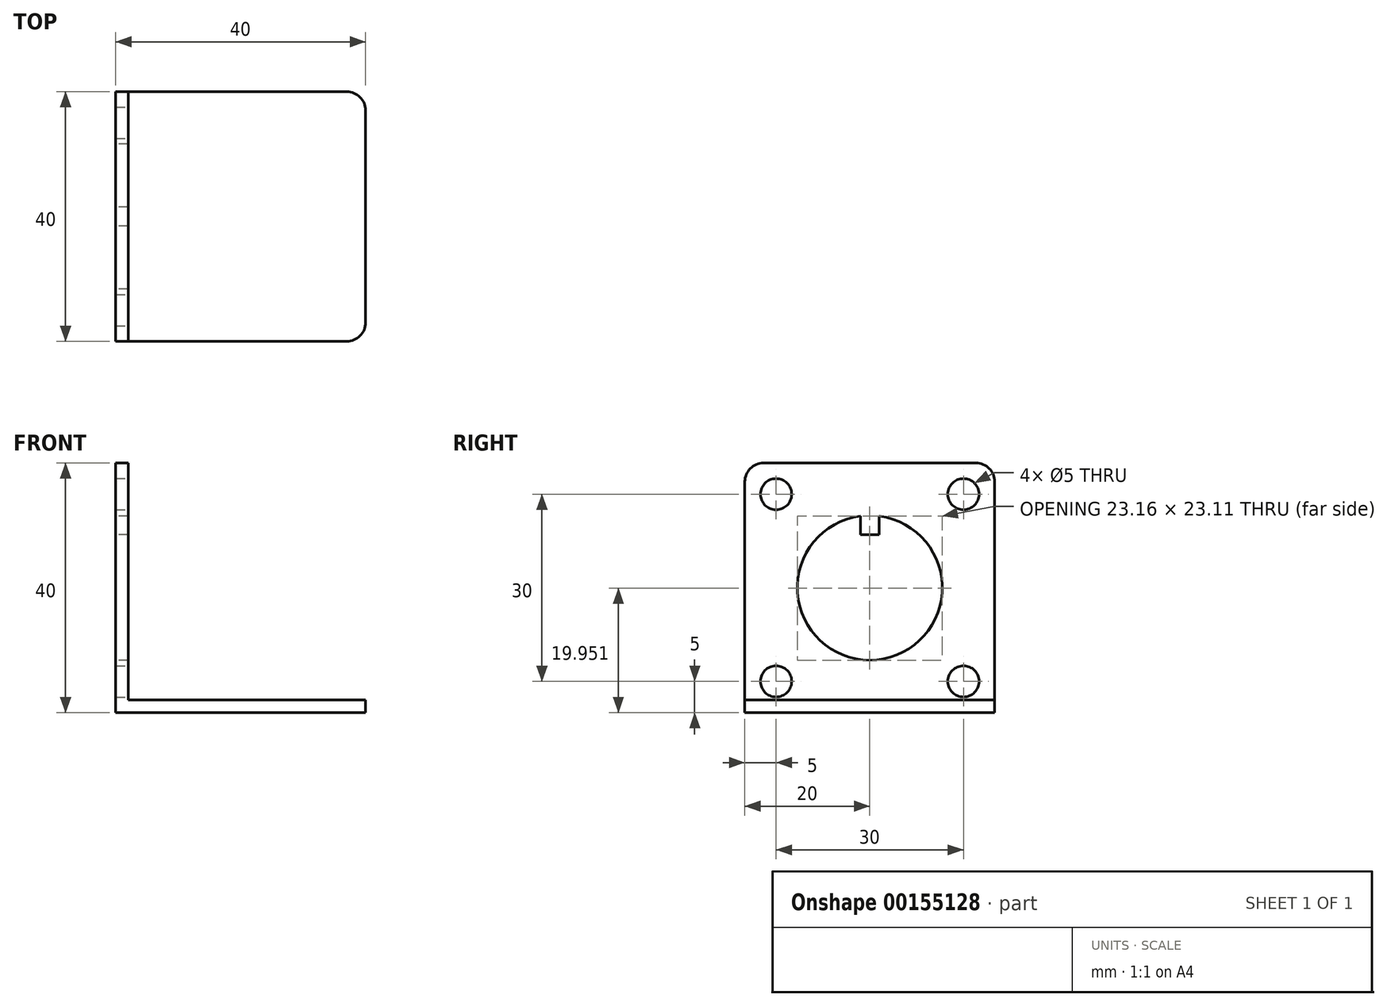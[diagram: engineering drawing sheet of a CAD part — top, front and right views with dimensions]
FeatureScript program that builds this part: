
annotation { "Feature Type Name" : "Feature", "Feature Type Description" : "" }
export const myFeature = defineFeature(function(context is Context, id is Id, definition is map)
    precondition{}
    {
        {
            var Q0;
            Q0=qCreatedBy(makeId("Front.planeOp"),FACE);
            var sketch = newSketch(context, id + "F0", { "sketchPlane" : qUnion([Q0])});
            skLineSegment(sketch, "E0", {"start": v(0, 0) * mm, "end": v(40, 0) * mm});
            skLineSegment(sketch, "E1", {"start": v(40, 0) * mm, "end": v(40, 2) * mm});
            skLineSegment(sketch, "E2", {"start": v(40, 2) * mm, "end": v(2, 2) * mm});
            skLineSegment(sketch, "E3", {"start": v(2, 2) * mm, "end": v(2, 40) * mm});
            skLineSegment(sketch, "E4", {"start": v(2, 40) * mm, "end": v(0, 40) * mm});
            skLineSegment(sketch, "E5", {"start": v(0, 40) * mm, "end": v(0, 0) * mm});
            skSolve(sketch);
        }
        {
            var Q0;
            Q0=makeQuery(id+"F0.imprint","IMPRINT",FACE,{"disambiguationData":[TD([[makeQuery(id+"F0.imprint","IMPRINT",EDGE,{"derivedFrom":sQuery(id+"F0.wireOp",EDGE,"E0")}),1.0]])]});
            extrude(context, id + "F1", {"entities" : qUnion([Q0]), "depth" : 40 * mm});
        }
        {
            var Q0;
            Q0=makeQuery(id+"F1.opExtrude","SWEPT_FACE",FACE,{"disambiguationData":[OSD([sQuery(id+"F0.wireOp",EDGE,"E5")])]});
            var sketch = newSketch(context, id + "F2", { "sketchPlane" : qUnion([Q0])});
            skLineSegment(sketch, "E6.bottom", {"start": v(0, 40) * mm, "end": v(5, 40) * mm, "construction": true});
            skLineSegment(sketch, "E6.top", {"start": v(0, 35) * mm, "end": v(5, 35) * mm, "construction": true});
            skLineSegment(sketch, "E6.left", {"start": v(0, 40) * mm, "end": v(0, 35) * mm, "construction": true});
            skLineSegment(sketch, "E6.right", {"start": v(5, 40) * mm, "end": v(5, 35) * mm, "construction": true});
            skLineSegment(sketch, "E7.bottom", {"start": v(40, 40) * mm, "end": v(35, 40) * mm, "construction": true});
            skLineSegment(sketch, "E7.top", {"start": v(40, 35) * mm, "end": v(35, 35) * mm, "construction": true});
            skLineSegment(sketch, "E7.left", {"start": v(40, 40) * mm, "end": v(40, 35) * mm, "construction": true});
            skLineSegment(sketch, "E7.right", {"start": v(35, 40) * mm, "end": v(35, 35) * mm, "construction": true});
            skLineSegment(sketch, "E8.bottom", {"start": v(0, 0) * mm, "end": v(5, 0) * mm, "construction": true});
            skLineSegment(sketch, "E8.top", {"start": v(0, 5) * mm, "end": v(5, 5) * mm, "construction": true});
            skLineSegment(sketch, "E8.left", {"start": v(0, 0) * mm, "end": v(0, 5) * mm, "construction": true});
            skLineSegment(sketch, "E8.right", {"start": v(5, 0) * mm, "end": v(5, 5) * mm, "construction": true});
            skLineSegment(sketch, "E9.bottom", {"start": v(40, 0) * mm, "end": v(35, 0) * mm, "construction": true});
            skLineSegment(sketch, "E9.top", {"start": v(40, 5) * mm, "end": v(35, 5) * mm, "construction": true});
            skLineSegment(sketch, "E9.left", {"start": v(40, 0) * mm, "end": v(40, 5) * mm, "construction": true});
            skLineSegment(sketch, "E9.right", {"start": v(35, 0) * mm, "end": v(35, 5) * mm, "construction": true});
            skSolve(sketch);
        }
        {
            var Q0;
            Q0=sQuery(id+"F2.wireOp",VERTEX,"E8.top.end");
            var Q1;
            Q1=sQuery(id+"F2.wireOp",VERTEX,"E6.top.end");
            var Q2;
            Q2=sQuery(id+"F2.wireOp",VERTEX,"E9.right.end");
            var Q3;
            Q3=sQuery(id+"F2.wireOp",VERTEX,"E7.right.end");
            var Q4;
            Q4=makeQuery(id+"F1.opExtrude","SWEPT_BODY",BODY,{"disambiguationData":[OSD([sQuery(id+"F0.wireOp",EDGE,"E0"),sQuery(id+"F0.wireOp",EDGE,"E1"),sQuery(id+"F0.wireOp",EDGE,"E2"),sQuery(id+"F0.wireOp",EDGE,"E3"),sQuery(id+"F0.wireOp",EDGE,"E4"),sQuery(id+"F0.wireOp",EDGE,"E5")])]});
            hole(context, id + "F3", {"style" : HoleStyle.SIMPLE, "endStyle" : HoleEndStyle.THROUGH, "holeDiameter" : 5 * mm, "locations" : qUnion([Q0, Q1, Q2, Q3]), "scope" : qUnion([Q4]), "isTappedThrough" : true, "startStyle" : HoleStartStyle.PART});
        }
        {
            var Q0;
            Q0=makeQuery(id+"F1.opExtrude","SWEPT_FACE",FACE,{"disambiguationData":[OSD([sQuery(id+"F0.wireOp",EDGE,"E5")])]});
            var sketch = newSketch(context, id + "F4", { "sketchPlane" : qUnion([Q0])});
            skLineSegment(sketch, "E10", {"start": v(0, 40) * mm, "end": v(40, 0) * mm, "construction": true});
            skLineSegment(sketch, "E11", {"start": v(0, 0) * mm, "end": v(40, 40) * mm, "construction": true});
            skArc(sketch, "E12", {"start": v(18.5, 31.5) * mm, "mid": v(20, 8.4) * mm, "end": v(21.5, 31.5) * mm});
            skLineSegment(sketch, "E13", {"start": v(20, 40) * mm, "end": v(20, 31.6) * mm, "construction": true});
            skLineSegment(sketch, "E14", {"start": v(20, 28.5) * mm, "end": v(21.5, 28.5) * mm});
            skLineSegment(sketch, "E15", {"start": v(21.5, 28.5) * mm, "end": v(21.5, 31.5) * mm});
            skLineSegment(sketch, "E16", {"start": v(20, 28.5) * mm, "end": v(18.5, 28.5) * mm});
            skLineSegment(sketch, "E17", {"start": v(18.5, 28.5) * mm, "end": v(18.5, 31.5) * mm});
            skLineSegment(sketch, "E18.trimOffspring", {"start": v(20, 28.5) * mm, "end": v(20, 0) * mm, "construction": true});
            skSolve(sketch);
        }
        {
            var Q0;
            Q0=makeQuery(id+"F4.imprint","IMPRINT",FACE,{"disambiguationData":[TD([[makeQuery(id+"F4.imprint","IMPRINT",EDGE,{"derivedFrom":sQuery(id+"F4.wireOp",EDGE,"E12")}),1.0]])]});
            extrude(context, id + "F5", {"entities" : qUnion([Q0]), "operationType" : NewBodyOperationType.REMOVE, "oppositeDirection" : true, "depth" : 20 * mm});
        }
        {
            var Q0;
            Q0=makeQuery(id+"F1.opExtrude","CAP_EDGE",EDGE,{"disambiguationData":[OSD([sQuery(id+"F0.wireOp",EDGE,"E4")])],"isStart":false});
            var Q1;
            Q1=makeQuery(id+"F1.opExtrude","CAP_EDGE",EDGE,{"disambiguationData":[OSD([sQuery(id+"F0.wireOp",EDGE,"E4")])],"isStart":true});
            var Q2;
            Q2=makeQuery(id+"F1.opExtrude","CAP_EDGE",EDGE,{"disambiguationData":[OSD([sQuery(id+"F0.wireOp",EDGE,"E1")])],"isStart":false});
            var Q3;
            Q3=makeQuery(id+"F1.opExtrude","CAP_EDGE",EDGE,{"disambiguationData":[OSD([sQuery(id+"F0.wireOp",EDGE,"E1")])],"isStart":true});
            fillet(context, id + "F6", {"entities" : qUnion([Q0, Q1, Q2, Q3]), "radius" : 3 * mm, "tangentPropagation" : true, "allowEdgeOverflow" : false});
        }
    });
